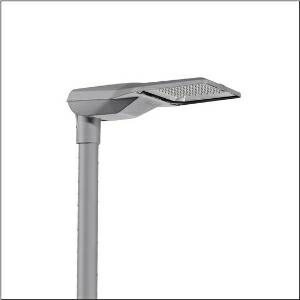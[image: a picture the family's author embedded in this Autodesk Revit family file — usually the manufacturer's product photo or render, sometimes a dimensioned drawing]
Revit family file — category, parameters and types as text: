
# Revit family: streetlight_sl_21_iq_midi___st0_8a_5xe3c31g08nb_0abe
name_source: partatom
category: Lighting Fixtures
units: mm (PartAtom-declared; Revit-internal decimal feet)

## family parameters
Cut with Voids When Loaded = No
Host = Face
Light Source = No
Part Type = Normal
Room Calculation Point = No
Round Connector Dimension = Use Diameter
Shared = No

## types (1)
- --- (1 x LED, 23230 lm, 155.5 W, 3000K)
    Apparent Load = 155 VA
    CIE Flux Codes = 41 75 97 100 100
    Color Rendering = 70
    Color Temperature = 3000K
    Default Elevation = 1800 mm
    Description = Streetlight SL 21 iQ midi, mast luminaire, primary light control with lens, of PMMA, primary optical cover: cover, of toughened safety glass, transparent, light distribution: ST0.8a, light emission: direct distribution, primary light characteristic: asymmetric, installation type: post-top, side-entry, LED, High Power LED, rated luminous flux: 23.230lm, luminous efficacy: 149lm/W, light colour: 730, colour temperature: 3000K, control gear: iQ Street-Remote, control: Street-Remote, Auto-Match, Temp-Guard, Lumen-Switch, Night-Set, Smart-Wire, Light-Fading, Desk-Remote (wireless, voltage-free reading and setting of iQ features in the workshop via application-optimized NFC function/RFID function), optimised constant luminous flux control (CLO 2.0), pre-setting: linear dimming characteristic, mains connection: 230..240V, AC, 50/60Hz, start of lifetime: 156W, end of service life: 162W, reduction: 69W, luminaire housing, of diecast aluminium, powder-coated, SITECO metallic grey (DB 702S), corrosivity category C5 high according to DIN EN ISO 12944, please order mast flange separately, inclination adjustable: 0°, 5°, 10°, 15°, sealing non-destructively replaceable, multi-level sealing system, length: 644mm, width: 335mm, height: 110mm, mast flange for spigot size: 42mm (side-entry): 5XC10008XM4, 60/48mm (side-entry/post-top): 5XC10108XM2, 76/60mm (side-entry/post-top): 5XC10108XM1, mounting height: 4..8m, protection rating (complete): IP66, insulation class (complete): insulation class II (safety insulation), certification: CE, ENEC, ENEC+, VDE, impact resistance: IK10, permissible operating ambient temperature for outdoor applications: -40..+50°C, standard-compliant lighting for roads and squares, packaging unit: 1 piece

Light Distribution: ST0.8a
    Height = 111 mm
    Lamp = 1 x LED
    Lamp Light Flux = 23230 lm
    Lamp Power = 155.5 W
    Lamp count = 1
    Length = 644 mm
    Luminous efficacy = 149 lm/W
    Manufacturer = Siteco
    ModVariant = No
    Model = 5XE3C31G08NB
    Number of Poles = 1
    OnlyDefault = Yes
    Power Factor = 1
    Product Name = Streetlight SL 21 iQ midi | ST0.8a
    Product group = mast luminaire | pylon top
    ProductGroupID = 6100
    Protection Class = Protection class II
    Protection Degree = IP 66
    RLX_Detail_Level = 1
    RLX_Emergency_Light_Flux = 0 lm
    RLX_Emergency_Type = 0
    RLX_Emergency_Type_DB = No
    RlxData = <blob elided: 27169 chars, md5=76b0efdf>
    Socket = socket
    Standby Power = 0 W
    System Light Flux = 23230 lm
    System Power = 155 W
    Type Comments = factory setting: luminous flux: 100 % | dim-lin: 254 | 823 mA
    Type Image = l_1004298.jpg
    URL = http://relux.com
    VarID = @adj_168433
    Voltage = 0 V
    Weight = 0.00 kg
    Width = 336 mm

## geometry (parser evidence)
native form markers: Blend x4, Sweep x13
no freeform markers — native parametric forms only
